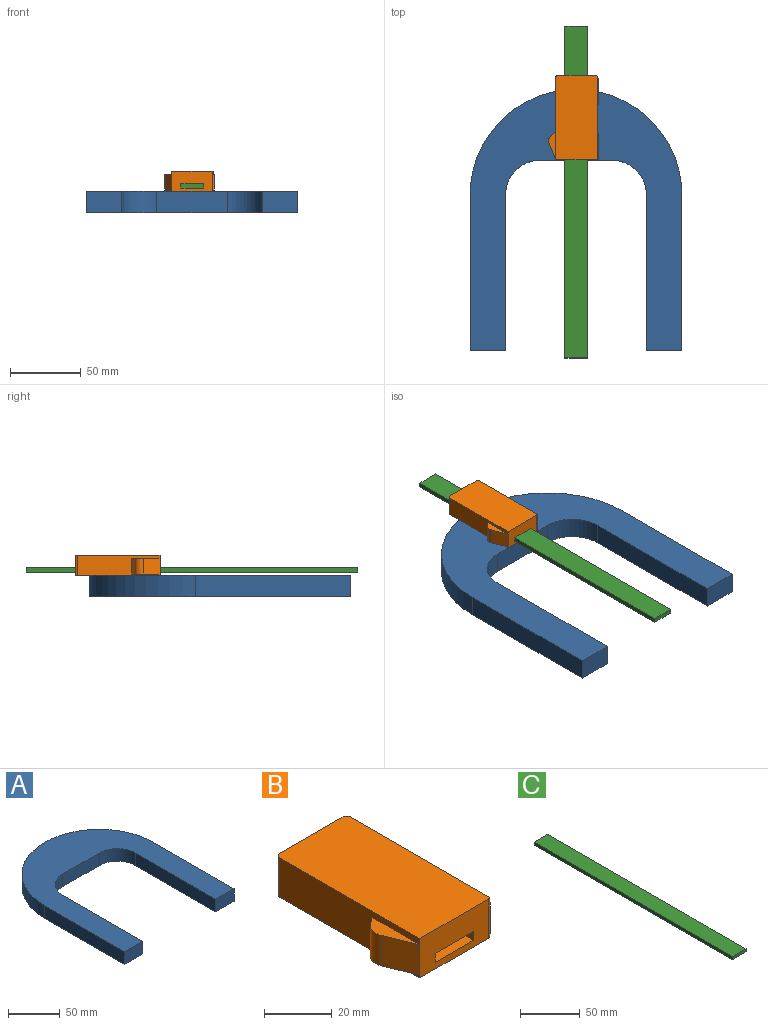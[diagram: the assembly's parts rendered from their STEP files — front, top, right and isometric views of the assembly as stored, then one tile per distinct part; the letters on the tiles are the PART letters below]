
ASSEMBLY  parts=3 mates=2
PART A: 12 faces, bbox 150x185x15 mm
  f0: plane 25x15mm, normal (0,-1,0), area 375mm2, adj f1,f9,f10,f11
  f1: plane 110x15mm, normal (1,0,0), area 1650mm2, adj f0,f2,f10,f11
  f2: cylinder r=25mm len=25mm, axis (0,0,-1), area 589mm2, adj f1,f3,f10,f11
  f3: plane 50x15mm, normal (0,-1,0), area 750mm2, adj f2,f4,f10,f11
  f4: cylinder r=25mm len=25mm, axis (0,0,-1), area 589mm2, adj f3,f5,f10,f11
  f5: plane 110x15mm, normal (-1,0,0), area 1650mm2, adj f4,f6,f10,f11
  f6: plane 25x15mm, normal (0,-1,0), area 375mm2, adj f5,f7,f10,f11
  f7: plane 110x15mm, normal (1,0,0), area 1650mm2, adj f6,f8,f10,f11
  f8: cylinder r=75mm len=150mm, axis (0,0,-1), area 3534.3mm2, adj f7,f9,f10,f11
  f9: plane 110x15mm, normal (-1,0,0), area 1650mm2, adj f0,f8,f10,f11
  f10: plane 185x150mm, normal (0,0,1), area 12104mm2, adj f0,f1,f2,f3,f4,f5,f6,f7
  f11: plane 185x150mm, normal (0,0,-1), area 12104mm2, adj f0,f1,f2,f3,f4,f5,f6,f7
PART B: 27 faces, bbox 35.2x60x14.2 mm
  f0: plane 58.5x14.2mm, normal (-1,0,0), area 610.7mm2, adj f1,f4,f5,f10,f13,f14,f25
  f1: plane 28.7x14.2mm, normal (0,-1,0), area 356.3mm2, adj f0,f4,f5,f6,f7,f8,f9,f12
  f2: plane 58.27x14.2mm, normal (1,0,0), area 412mm2, adj f4,f5,f15,f17,f18,f19,f21,f22
  f3: plane 26.5x14.2mm, normal (0,1,0), area 325.1mm2, adj f4,f5,f6,f7,f8,f9,f24,f25
  f4: plane 60x29.5mm, normal (0,0,1), area 1769mm2, adj f0,f1,f2,f3,f24,f25,f26
  f5: plane 60x29.5mm, normal (0,0,-1), area 1769mm2, adj f0,f1,f2,f3,f24,f25,f26
  f6: plane 60x3.2mm, normal (1,0,0), area 192mm2, adj f1,f3,f7,f9
  f7: plane 60x16mm, normal (0,0,1), area 960mm2, adj f1,f3,f6,f8
  f8: plane 60x3.2mm, normal (-1,0,0), area 192mm2, adj f1,f3,f7,f9
  f9: plane 60x16mm, normal (0,0,-1), area 960mm2, adj f1,f3,f6,f8
  f10: plane 11x3.21mm, normal (-0.64,0.77,0), area 46mm2, adj f0,f11,f13,f14
  f11: cylinder r=5mm len=11mm, axis (0,0,-1), area 69.1mm2, adj f10,f12,f13,f14
  f12: plane 11.63x11mm, normal (-0.93,-0.37,0), area 137.8mm2, adj f1,f11,f13,f14
  f13: plane 20x5.01mm, normal (0,0,1), area 57.5mm2, adj f0,f10,f11,f12
  f14: plane 20x5.01mm, normal (0,0,-1), area 57.5mm2, adj f0,f10,f11,f12
  f15: plane 11x0.7mm, normal (0,-1,0), area 7.7mm2, adj f2,f16,f18,f19
  f16: plane 19x11mm, normal (1,0,0), area 209mm2, adj f15,f17,f18,f19
  f17: plane 11x0.7mm, normal (0,1,0), area 7.7mm2, adj f2,f16,f18,f19
  f18: plane 19x0.7mm, normal (0,0,1), area 13.3mm2, adj f2,f15,f16,f17
  f19: plane 19x0.7mm, normal (0,0,-1), area 13.3mm2, adj f2,f15,f16,f17
  f20: plane 17.5x11mm, normal (1,0,0), area 192.5mm2, adj f21,f22,f23,f26
  f21: plane 11x0.7mm, normal (0,1,0), area 7.7mm2, adj f2,f20,f22,f23
  f22: plane 18.77x0.7mm, normal (0,0,1), area 12.9mm2, adj f2,f20,f21,f26
  f23: plane 18.77x0.7mm, normal (0,0,-1), area 12.9mm2, adj f2,f20,f21,f26
  f24: cylinder r=1.5mm len=14.2mm, axis (0,0,-1), area 33.5mm2, adj f2,f3,f4,f5
  f25: cylinder r=1.5mm len=14.2mm, axis (0,0,-1), area 33.5mm2, adj f0,f3,f4,f5
  f26: cylinder r=1.5mm len=14.2mm, axis (0,0,1), area 28.6mm2, adj f1,f2,f4,f5,f20,f22,f23
PART C: 6 faces, bbox 16x235x3.2 mm
  f0: plane 235x3.2mm, normal (-1,0,0), area 752mm2, adj f1,f3,f4,f5
  f1: plane 16x3.2mm, normal (0,-1,0), area 51.2mm2, adj f0,f2,f4,f5
  f2: plane 235x3.2mm, normal (1,0,0), area 752mm2, adj f1,f3,f4,f5
  f3: plane 16x3.2mm, normal (0,1,0), area 51.2mm2, adj f0,f2,f4,f5
  f4: plane 235x16mm, normal (0,0,1), area 3760mm2, adj f0,f1,f2,f3
  f5: plane 235x16mm, normal (0,0,-1), area 3760mm2, adj f0,f1,f2,f3
PLACE A at identity fixed
PLACE B t=(-14.35,0,15)mm
PLACE C t=(-7.85,-140.15,17.4)mm
MATE slider B.f1 <-> C.f1  axis (0,-1,0) through (0.15,0,20.6)mm
MATE fastened A.f10 <-> B.f5  axis (0,0,1) through (0,0,15)mm
